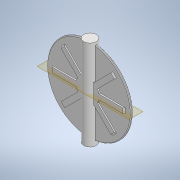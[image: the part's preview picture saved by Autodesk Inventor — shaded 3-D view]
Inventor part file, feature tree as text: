
AUTODESK INVENTOR PART (.ipt)
format: ipt  version: 2020.2 (Build 242310000, 310)  size: 287,744 bytes
history: native  units: mm
features: extrude x4, sketch x4, chamfer x1, mirror x1, fillet x1
ambient origin geometry x8: Origin, YZ Plane, XZ Plane, XY Plane, X Axis, Y Axis, Z Axis, Center Point
bodies: Solid1 (feature_tree)
feature tree (11):
  extrude  "Extrusion1"  Depth=5.0mm TaperAngle=0.0deg
  extrude  "Extrusion2"  Depth=109.5mm TaperAngle=0.0deg
  extrude  "Extrusion3"  Depth=60.0mm
  chamfer  "Chamfer1"  Angle=360.0deg  [1 undecoded]
  mirror  "Mirror2"
  fillet  "Fillet2"  Radius=3.0mm
  extrude  "Extrusion5"  Depth=15.0mm
  sketch  "Sketch1"  dims[d0=200.0mm d1=5.0mm d2=0.0mm]
  sketch  "Sketch2"  dims[d3=29.6mm d4=105.5mm d5=109.5mm d6=0.0mm d7=0.0mm]
  sketch  "Sketch3"  dims[d10=6.0mm d12=60.0mm]
  sketch  "Sketch6"  dims[d13=3.454961mm d16=360.0deg d18=3.0mm d19=0.0mm d23=5.0mm d24=2.5mm d25=0.0mm d26=3.0mm d27=2.0mm d28=45.0deg d29=1.5mm d33=0.2mm d34=15.0mm d35=0.0mm]
note: 1 required parameter value undecoded (feature->parameter linkage not recoverable at this tier; creation-order binding heuristic only, values carry confidence <= 0.55)
